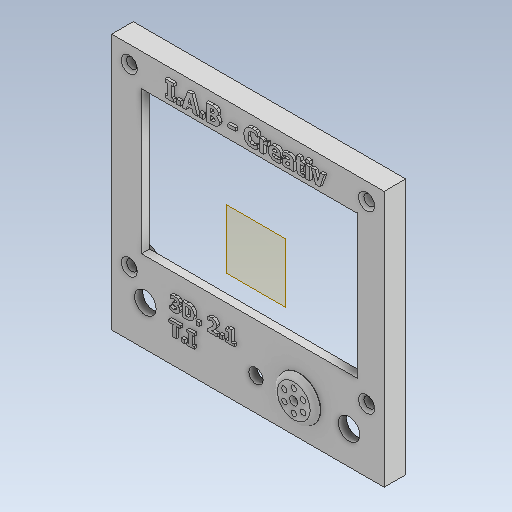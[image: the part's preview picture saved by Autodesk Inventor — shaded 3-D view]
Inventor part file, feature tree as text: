
AUTODESK INVENTOR PART (.ipt)
format: ipt  version: 2020 (Build 240168000, 168)  size: 651,264 bytes
history: native  units: mm
features: sketch x10, reference x9, extrude x6, hole x4, other x3, fillet x2, plane x1, pattern_circular x1
ambient origin geometry x8: Origin, YZ Plane, XZ Plane, XY Plane, X Axis, Y Axis, Z Axis, Center Point
bodies: Solid1 (feature_tree)
feature tree (36):
  extrude  "Extrusion1"  Depth=95.0mm
  plane  "Work Plane1"
  hole  "Hole1"  [1 undecoded]
  extrude  "Extrusion5"  Depth=10.0mm
  extrude  "Extrusion6"  Depth=3.0mm
  extrude  "Extrusion7"  Depth=1.0mm
  hole  "Hole2"  [1 undecoded]
  hole  "Hole3"  [1 undecoded]
  pattern_circular  "Circular Pattern1"  [2 undecoded]
  fillet  "Fillet2"  Radius=60.0mm
  hole  "Hole4"  [1 undecoded]
  extrude  "Extrusion8"  Depth=1.0mm TaperAngle=0.0deg
  extrude  "Extrusion9"  Depth=8.0mm
  fillet  "Fillet3"  Radius=4.0mm
  sketch  "Sketch1"  dims[d0=95.0mm d1=101.0mm]
  sketch  "Sketch4"  dims[d2=8.0mm d3=0.0mm d11=10.0mm]
  sketch  "Sketch5"  dims[d12=10.0mm d13=10.0mm]
  reference  "Reference13"
  sketch  "Sketch6"  dims[d14=10.0mm]
  reference  "Reference14"
  reference  "Reference15"
  reference  "Reference16"
  reference  "Reference17"
  reference  "Reference18"
  reference  "Reference19"
  reference  "Reference20"
  reference  "Reference21"
  sketch  "Sketch7"  dims[d18=4.0mm d19=6.0mm d20=4.0mm d21=2.0mm d22=90.0deg d23=8.0mm d24=20.594885mm d25=3.0mm]
  sketch  "Sketch8"  dims[d26=5.0mm d27=0.0mm d29=1.0mm]
  sketch  "Sketch9"  dims[d30=1.0mm d31=1.0mm]
  sketch  "Sketch10"  dims[d32=0.0mm d33=0.0mm d35=1.0mm]
  sketch  "Sketch11"  dims[d36=1.0mm]
  sketch  "Sketch12"  dims[d37=2.0mm d38=0.0mm d39=3.0mm d40=6.0mm d41=4.0mm d42=2.0mm d43=90.0deg d44=8.0mm d45=20.594885mm d46=4.0mm d47=2.0mm d48=6.0mm d49=4.0mm d50=2.0mm d51=90.0deg d52=8.0mm d53=20.594885mm d54=60.0mm d55=360.0deg d57=1.9mm d58=4.0mm d59=6.0mm d60=6.0mm d61=2.0mm d62=90.0deg d63=8.0mm d64=20.594885mm d65=1.0mm d66=0.0mm d67=8.0mm d68=4.0mm d69=0.0mm d70=2.0mm d71=14.0mm d72=16.0mm]
  other  "0008-10-11 ansamblu display.iam"
  other  "0008-10-039 carcasa spate:1"
  other  "10-06-03 ReprapDiscountFullGraphicSmartController-Robotale_Dummy:1"
note: 6 required parameter values undecoded (feature->parameter linkage not recoverable at this tier; creation-order binding heuristic only, values carry confidence <= 0.55)
